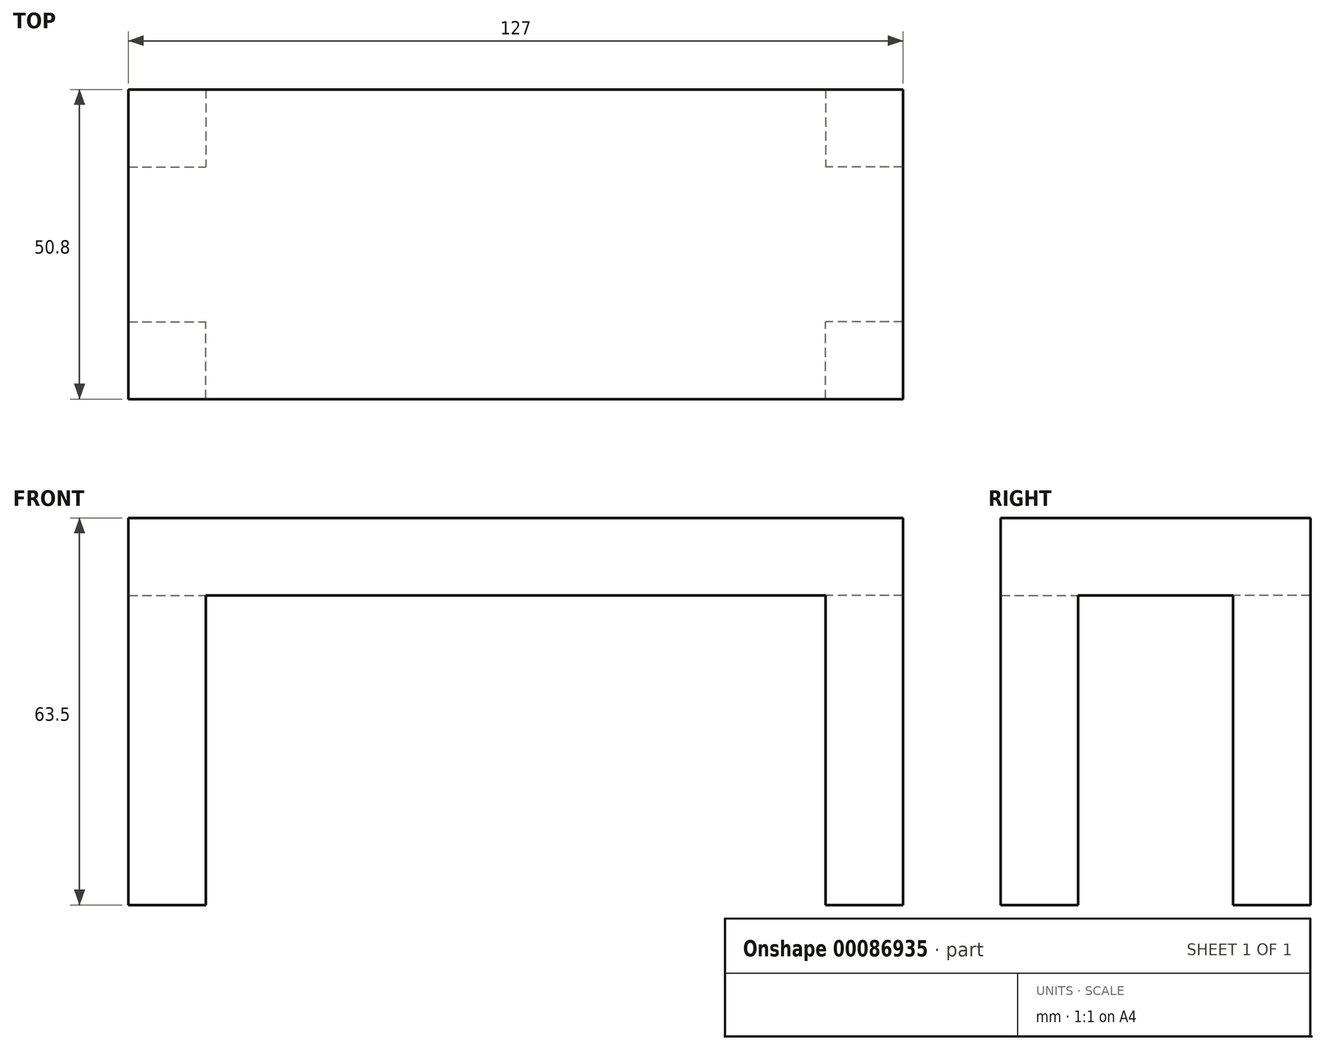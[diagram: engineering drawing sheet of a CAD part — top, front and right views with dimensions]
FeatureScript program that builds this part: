
annotation { "Feature Type Name" : "Feature", "Feature Type Description" : "" }
export const myFeature = defineFeature(function(context is Context, id is Id, definition is map)
    precondition{}
    {
        {
            var Q0;
            Q0=qCreatedBy(makeId("Top.planeOp"),FACE);
            var sketch = newSketch(context, id + "F0", { "sketchPlane" : qUnion([Q0])});
            skLineSegment(sketch, "E0.bottom", {"start": v(63.5, 25.4) * mm, "end": v(-63.5, 25.4) * mm});
            skLineSegment(sketch, "E0.top", {"start": v(63.5, -25.4) * mm, "end": v(-63.5, -25.4) * mm});
            skLineSegment(sketch, "E0.left", {"start": v(63.5, 25.4) * mm, "end": v(63.5, -25.4) * mm});
            skLineSegment(sketch, "E0.right", {"start": v(-63.5, 25.4) * mm, "end": v(-63.5, -25.4) * mm});
            skPoint(sketch, "E0.middle", {"position": v(0, 0) * mm});
            skSolve(sketch);
        }
        {
            var Q0;
            Q0=makeQuery(id+"F0.imprint","IMPRINT",FACE,{"disambiguationData":[TD([[makeQuery(id+"F0.imprint","IMPRINT",EDGE,{"derivedFrom":sQuery(id+"F0.wireOp",EDGE,"E0.bottom")}),1.0]])]});
            extrude(context, id + "F1", {"entities" : qUnion([Q0]), "depth" : 12.7 * mm});
        }
        {
            var Q0;
            Q0=makeQuery(id+"F1.opExtrude","CAP_FACE",FACE,{"disambiguationData":[OSD([sQuery(id+"F0.wireOp",EDGE,"E0.bottom"),sQuery(id+"F0.wireOp",EDGE,"E0.top"),sQuery(id+"F0.wireOp",EDGE,"E0.left"),sQuery(id+"F0.wireOp",EDGE,"E0.right")])],"isStart":true});
            var sketch = newSketch(context, id + "F2", { "sketchPlane" : qUnion([Q0])});
            skLineSegment(sketch, "E1.bottom", {"start": v(-63.5, -25.4) * mm, "end": v(-50.8, -25.4) * mm});
            skLineSegment(sketch, "E1.top", {"start": v(-63.5, -12.7) * mm, "end": v(-50.8, -12.7) * mm});
            skLineSegment(sketch, "E1.left", {"start": v(-63.5, -25.4) * mm, "end": v(-63.5, -12.7) * mm});
            skLineSegment(sketch, "E1.right", {"start": v(-50.8, -25.4) * mm, "end": v(-50.8, -12.7) * mm});
            skLineSegment(sketch, "E2.bottom", {"start": v(-63.5, 25.4) * mm, "end": v(-50.8, 25.4) * mm});
            skLineSegment(sketch, "E2.top", {"start": v(-63.5, 12.7) * mm, "end": v(-50.8, 12.7) * mm});
            skLineSegment(sketch, "E2.left", {"start": v(-63.5, 25.4) * mm, "end": v(-63.5, 12.7) * mm});
            skLineSegment(sketch, "E2.right", {"start": v(-50.8, 25.4) * mm, "end": v(-50.8, 12.7) * mm});
            skLineSegment(sketch, "E3.bottom", {"start": v(63.5, 25.4) * mm, "end": v(50.8, 25.4) * mm});
            skLineSegment(sketch, "E3.top", {"start": v(63.5, 12.7) * mm, "end": v(50.8, 12.7) * mm});
            skLineSegment(sketch, "E3.left", {"start": v(63.5, 25.4) * mm, "end": v(63.5, 12.7) * mm});
            skLineSegment(sketch, "E3.right", {"start": v(50.8, 25.4) * mm, "end": v(50.8, 12.7) * mm});
            skLineSegment(sketch, "E4.bottom", {"start": v(63.5, -25.4) * mm, "end": v(50.8, -25.4) * mm});
            skLineSegment(sketch, "E4.top", {"start": v(63.5, -12.7) * mm, "end": v(50.8, -12.7) * mm});
            skLineSegment(sketch, "E4.left", {"start": v(63.5, -25.4) * mm, "end": v(63.5, -12.7) * mm});
            skLineSegment(sketch, "E4.right", {"start": v(50.8, -25.4) * mm, "end": v(50.8, -12.7) * mm});
            skSolve(sketch);
        }
        {
            var Q0;
            Q0=makeQuery(id+"F2.imprint","IMPRINT",FACE,{"disambiguationData":[TD([[makeQuery(id+"F2.imprint","IMPRINT",EDGE,{"derivedFrom":sQuery(id+"F2.wireOp",EDGE,"E1.bottom")}),-1.0]])]});
            var Q1;
            Q1=makeQuery(id+"F2.imprint","IMPRINT",FACE,{"disambiguationData":[TD([[makeQuery(id+"F2.imprint","IMPRINT",EDGE,{"derivedFrom":sQuery(id+"F2.wireOp",EDGE,"E2.bottom")}),1.0]])]});
            var Q2;
            Q2=makeQuery(id+"F2.imprint","IMPRINT",FACE,{"disambiguationData":[TD([[makeQuery(id+"F2.imprint","IMPRINT",EDGE,{"derivedFrom":sQuery(id+"F2.wireOp",EDGE,"E3.bottom")}),1.0]])]});
            var Q3;
            Q3=makeQuery(id+"F2.imprint","IMPRINT",FACE,{"disambiguationData":[TD([[makeQuery(id+"F2.imprint","IMPRINT",EDGE,{"derivedFrom":sQuery(id+"F2.wireOp",EDGE,"E4.bottom")}),-1.0]])]});
            extrude(context, id + "F3", {"entities" : qUnion([Q0, Q1, Q2, Q3]), "operationType" : NewBodyOperationType.ADD, "depth" : 50.8 * mm});
        }
    });
